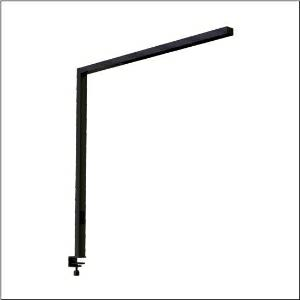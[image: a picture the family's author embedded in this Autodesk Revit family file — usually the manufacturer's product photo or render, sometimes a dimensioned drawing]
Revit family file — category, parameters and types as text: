
# Revit family: silica_31_desk_51my52ga4cb
name_source: partatom
category: Lighting Fixtures
units: mm (PartAtom-declared; Revit-internal decimal feet)

## family parameters
Cut with Voids When Loaded = No
Host = Face
Light Source = No
Part Type = Normal
Room Calculation Point = No
Round Connector Dimension = Use Diameter
Shared = No

## types (1)
- Silica 31 Desk (1 x LED, 10600 lm, 75 W, 4000K)
    Apparent Load = 75 VA
    CIE Flux Codes = 86 100 100 24 100
    Color Rendering = 80
    Color Temperature = 4000K
    Default Elevation = 1800 mm
    Description = Silica® 31 Desk, desktop luminaire, secondary optical cover: cover panel, of PMMA, light emission: direct/indirect distribution, primary light characteristic: symmetric, installation type: as desk luminaire, LED, rated luminous flux: 10.600lm, luminous efficacy: 141lm/W, light colour: 840, colour temperature: 4000K, control gear: Touchdim, daylight-dependent control, with cable with plug, mains connection: 230V, AC, 50Hz, connection cable included, cable length: 2,5m, rated input power: 75W, luminaire head, of aluminium, jet black (RAL 9005), length: 1.203mm, width: 52mm, supporting column, angular, of aluminium, jet black (RAL 9005), baseplate, of steel, jet black (RAL 9005), local control - self-sufficient standalone sensors, direct and indirect component separately switchable, protection rating (complete): IP20, insulation class (complete): insulation class I (protective earthing), certification: CE, ENEC, permissible operating ambient temperature: -20..+40°C, standard: EN 50419, packaging unit: 1 piece
    Height = 36 mm
    Lamp = 1 x LED
    Lamp Light Flux = 10600 lm
    Lamp Power = 75 W
    Lamp count = 1
    Length = 1203 mm
    Luminous efficacy = 141 lm/W
    Manufacturer = Siteco
    ModVariant = No
    Model = 51MY52GA4CB
    Mounting Place = Floor
    Mounting Type = Freestanding
    Number of Poles = 1
    OnlyDefault = Yes
    Power Factor = 1
    Product Name = Silica 31 Desk
    Product group = desktop luminaire
    ProductGroupID = 1303
    Protection Class = Protection class I
    Protection Degree = IP 20
    RLX_Detail_Level = 1
    RLX_Emergency_Light_Flux = 0 lm
    RLX_Emergency_Type = 0
    RLX_Emergency_Type_DB = No
    RlxData = <blob elided: 19305 chars, md5=81318885>
    Socket = socket
    Standby Power = 0 W
    System Light Flux = 10600 lm
    System Power = 75 W
    Type Comments = Product without accessories
    Type Image = l_1275329.jpg
    URL = http://relux.com
    VarID = ---
    Voltage = 0 V
    Weight = 0.00 kg
    Width = 52 mm  [stored 0.170604 ft]

note: [stored X ft] marks values corroborated as IEEE doubles in the binary element streams (Revit-internal decimal feet)

## geometry (parser evidence)
native form markers: Blend x4, Sweep x16
no freeform markers — native parametric forms only
